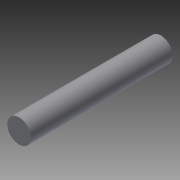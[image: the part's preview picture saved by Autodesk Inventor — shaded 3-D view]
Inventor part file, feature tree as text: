
AUTODESK INVENTOR PART (.ipt)
format: ipt  version: 2014 (Build 180170000, 170)  size: 68,608 bytes
history: native  units: in
note: dims shown in document units (in); Inventor stores cm internally (conversion verified against a paired STEP export)
features: extrude x1, sketch x1
ambient origin geometry x8: Origin, YZ Plane, XZ Plane, XY Plane, X Axis, Y Axis, Z Axis, Center Point
bodies: Solid1 (feature_tree)
feature tree (2):
  extrude  "Extrusion1"  Depth=1.5in TaperAngle=0.0deg
  sketch  "Sketch1"  dims[d0=0.25in d1=1.5in d2=0.0in]
